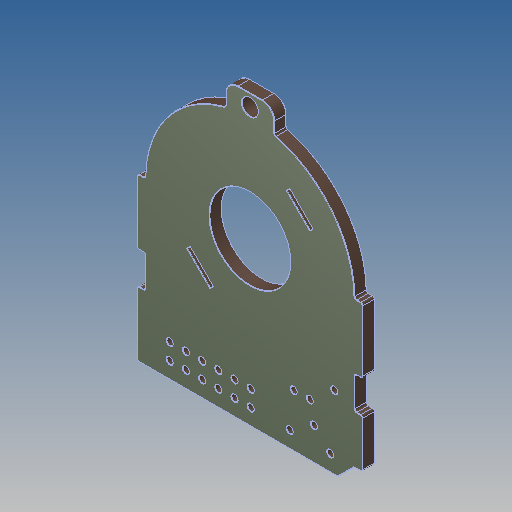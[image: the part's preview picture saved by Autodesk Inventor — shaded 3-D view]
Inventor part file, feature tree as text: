
AUTODESK INVENTOR PART (.ipt)
format: ipt  version: 2020 (Build 240168000, 168)  size: 282,624 bytes
history: mixed  units: mm
features: other x1, fillet x1, imported_body x1
ambient origin geometry x8: Origin, YZ Plane, XZ Plane, XY Plane, X Axis, Y Axis, Z Axis, Center Point
bodies: Body1 (imported_parasolid)
feature tree (3):
  other  "Твердое тело1"
  fillet  "Fillet1"  [1 undecoded]
  imported_body  NMx_Import_Brep_tag  [imported B-rep: ~179 faces, bbox_mm=[27.8, 35.546314, 1.5]]
note: 1 required parameter value undecoded (feature->parameter linkage not recoverable at this tier; creation-order binding heuristic only, values carry confidence <= 0.55)
